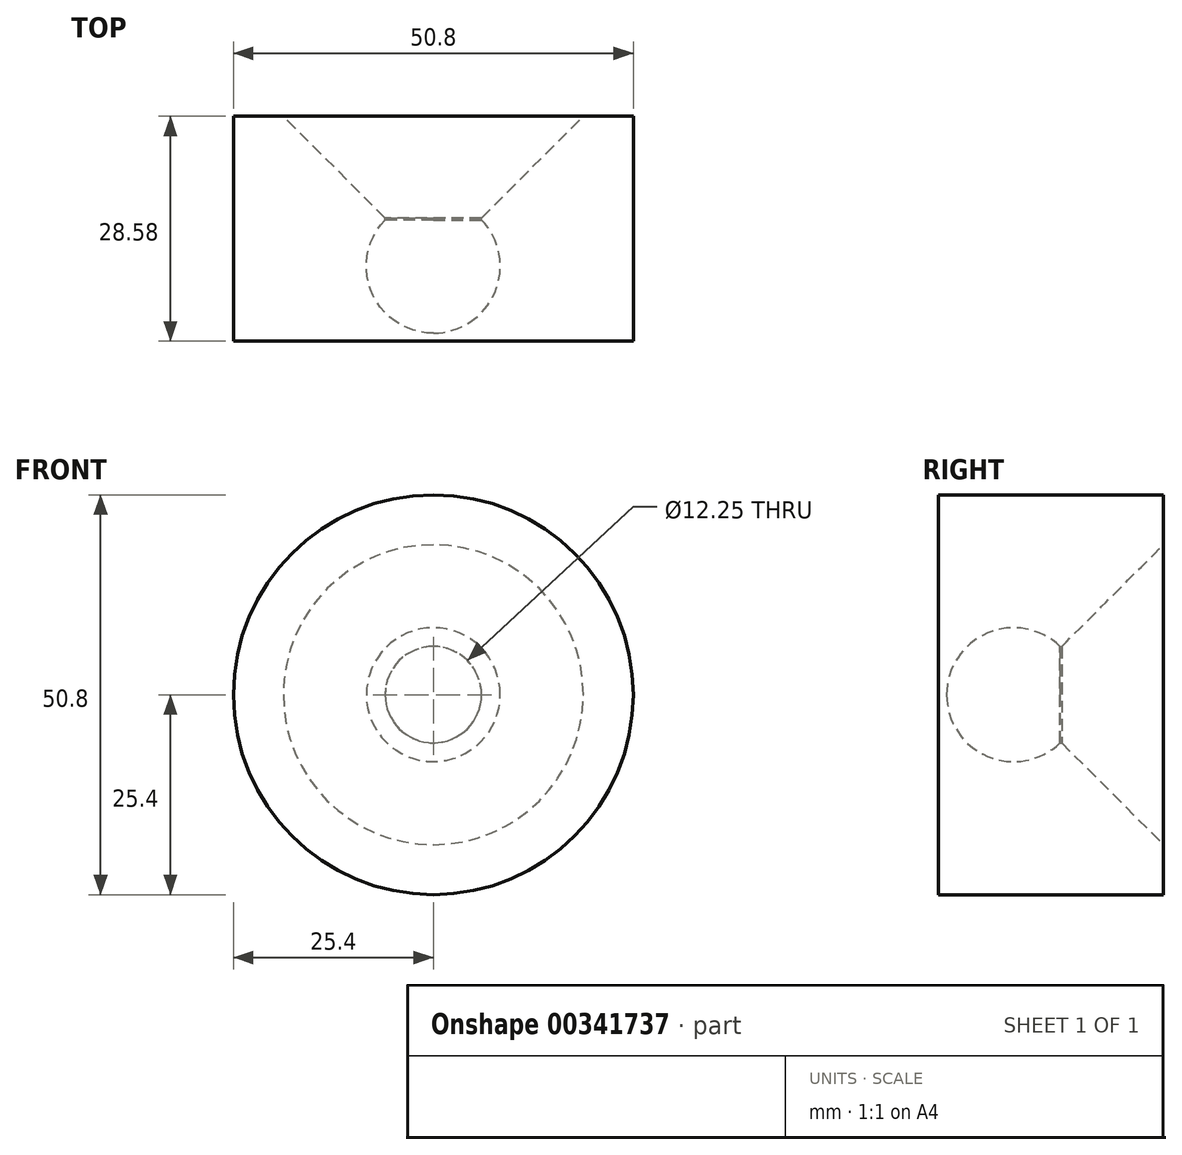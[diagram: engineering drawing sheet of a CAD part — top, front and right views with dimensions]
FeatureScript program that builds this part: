
annotation { "Feature Type Name" : "Feature", "Feature Type Description" : "" }
export const myFeature = defineFeature(function(context is Context, id is Id, definition is map)
    precondition{}
    {
        {
            var Q0;
            Q0=qCreatedBy(makeId("Top.planeOp"),FACE);
            var sketch = newSketch(context, id + "F0", { "sketchPlane" : qUnion([Q0])});
            skLineSegment(sketch, "E0", {"start": v(0, 0) * mm, "end": v(-25.4, 0) * mm});
            skLineSegment(sketch, "E1", {"start": v(-25.4, 0) * mm, "end": v(-25.4, 28.58) * mm});
            skLineSegment(sketch, "E2", {"start": v(0, 9.53) * mm, "end": v(0, 0) * mm});
            skLineSegment(sketch, "E3", {"start": v(-25.4, 28.58) * mm, "end": v(-19.05, 28.58) * mm});
            skLineSegment(sketch, "E4", {"start": v(-19.05, 28.58) * mm, "end": v(0, 9.53) * mm});
            skArc(sketch, "E5", {"start": v(0, 1.03) * mm, "mid": v(-7.85, 6.27) * mm, "end": v(-6.01, 15.54) * mm});
            skSolve(sketch);
        }
        {
            var Q0;
            {var subQ2=sQuery(id+"F0.wireOp",EDGE,"E0");Q0=makeQuery(id+"F0.imprint","IMPRINT",FACE,{"disambiguationData":[TD([[makeQuery(id+"F0.imprint","IMPRINT",EDGE,{"derivedFrom":subQ2}),-1.0]])]});}
            var Q1;
            Q1=sQuery(id+"F0.wireOp",EDGE,"E2");
            revolve(context, id + "F1", {"entities" : qUnion([Q0]), "axis" : qUnion([Q1]), "revolveType" : RevolveType.FULL});
        }
        {
            var Q0;
            Q0=makeQuery(id+"F1.opRevolve","SWEPT_FACE",FACE,{"disambiguationData":[OSD([sQuery(id+"F0.wireOp",EDGE,"E3")])]});
            var sketch = newSketch(context, id + "F2", { "sketchPlane" : qUnion([Q0])});
            skCircle(sketch, "E6", {"center": v(0, 0) * mm, "radius": 6.12 * mm});
            skSolve(sketch);
        }
        {
            var Q0;
            Q0 = qSketchRegion(id + "F2", true);
            extrude(context, id + "F3", {"entities" : qUnion([Q0]), "operationType" : NewBodyOperationType.REMOVE, "oppositeDirection" : true, "depth" : 14.7 * mm});
        }
    });
